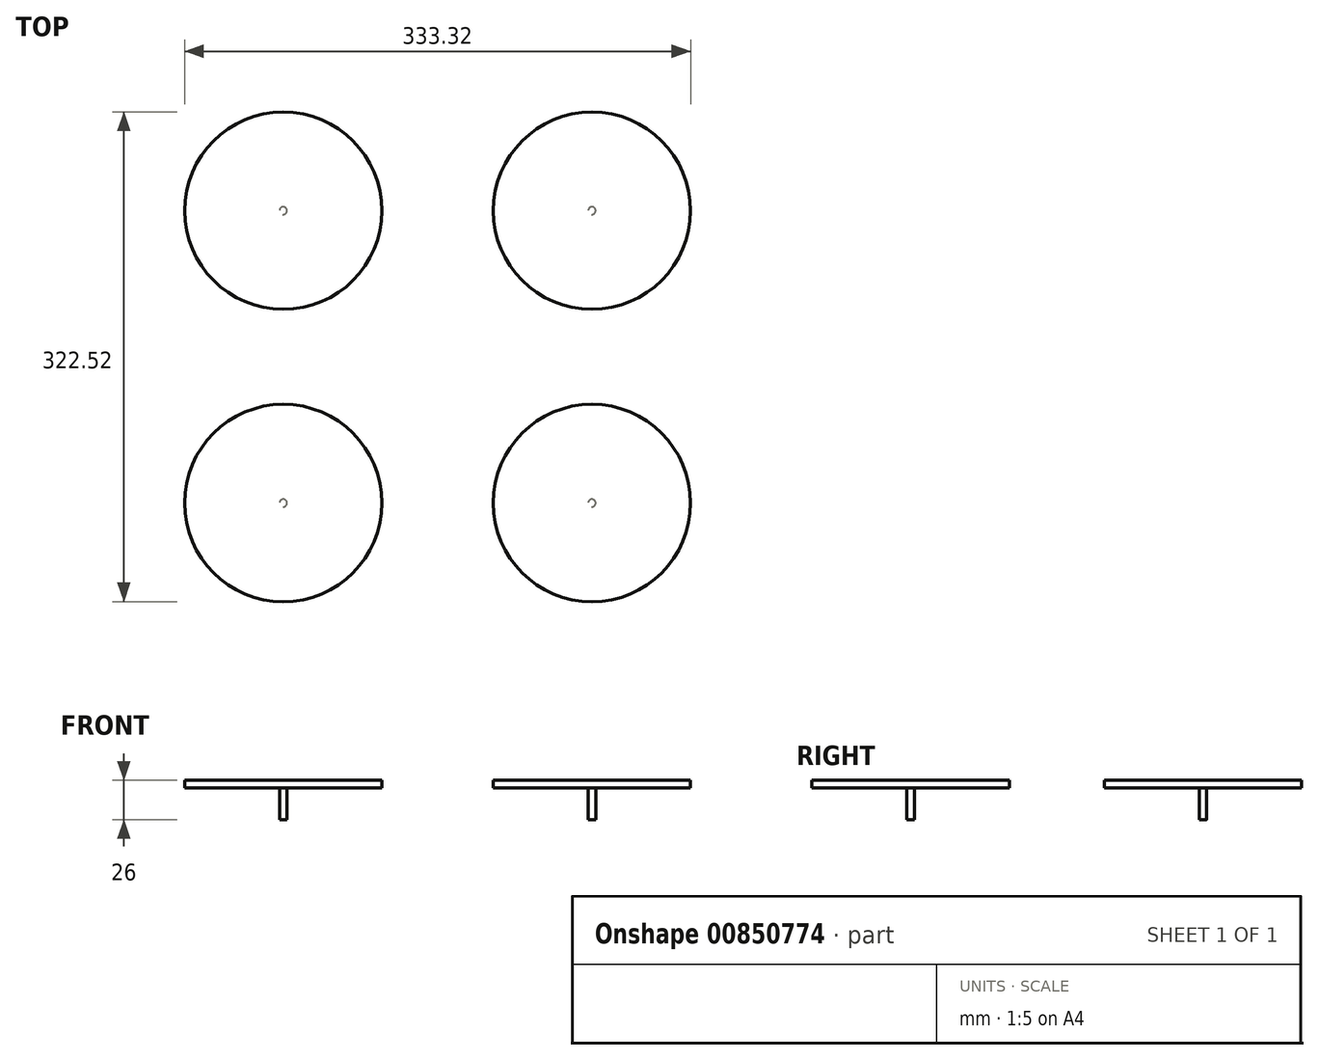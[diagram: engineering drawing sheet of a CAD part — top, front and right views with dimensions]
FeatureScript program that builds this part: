
annotation { "Feature Type Name" : "Feature", "Feature Type Description" : "" }
export const myFeature = defineFeature(function(context is Context, id is Id, definition is map)
    precondition{}
    {
        {
            var Q0;
            Q0=qCreatedBy(makeId("Top.planeOp"),FACE);
            var sketch = newSketch(context, id + "F0", { "sketchPlane" : qUnion([Q0])});
            skLineSegment(sketch, "E0", {"start": v(0, 0) * mm, "end": v(101.66, 96.26) * mm, "construction": true});
            skCircle(sketch, "E1", {"center": v(101.66, 96.26) * mm, "radius": 2.5 * mm});
            skSolve(sketch);
        }
        {
            var Q0;
            Q0=qSketchRegion(id+"F0",true);
            extrude(context, id + "F1", {"entities" : qUnion([Q0]), "depth" : 21 * mm, "offsetDistance" : 25 * mm});
        }
        {
            var Q0;
            Q0=makeQuery(id+"F1.opExtrude","CAP_FACE",FACE,{"disambiguationData":[OSD([sQuery(id+"F0.wireOp",EDGE,"E1")])],"isStart":false});
            var sketch = newSketch(context, id + "F2", { "sketchPlane" : qUnion([Q0])});
            skCircle(sketch, "E2", {"center": v(101.66, 96.26) * mm, "radius": 65 * mm});
            skSolve(sketch);
        }
        {
            var Q0;
            Q0=qSketchRegion(id+"F2",true);
            extrude(context, id + "F3", {"entities" : qUnion([Q0]), "operationType" : NewBodyOperationType.ADD, "depth" : 5 * mm, "offsetDistance" : 25 * mm});
        }
        {
            var Q0;
            Q0=makeQuery(id+"F1.opExtrude","SWEPT_BODY",BODY,{"disambiguationData":[OSD([sQuery(id+"F0.wireOp",EDGE,"E1")])]});
            var Q1;
            Q1=qCreatedBy(makeId("Right.planeOp"),FACE);
            mirror(context, id + "F4", {"entities" : qUnion([Q0]), "mirrorPlane" : qUnion([Q1])});
        }
        {
            var Q0;
            Q0=makeQuery(id+"F4.opPattern","COPY",BODY,{"derivedFrom":makeQuery(id+"F1.opExtrude","SWEPT_BODY",BODY,{"disambiguationData":[OSD([sQuery(id+"F0.wireOp",EDGE,"E1")])]}),"instanceName":"1"});
            var Q1;
            Q1=makeQuery(id+"F1.opExtrude","SWEPT_BODY",BODY,{"disambiguationData":[OSD([sQuery(id+"F0.wireOp",EDGE,"E1")])]});
            var Q2;
            Q2=qCreatedBy(makeId("Front.planeOp"),FACE);
            mirror(context, id + "F5", {"entities" : qUnion([Q0, Q1]), "mirrorPlane" : qUnion([Q2])});
        }
    });
